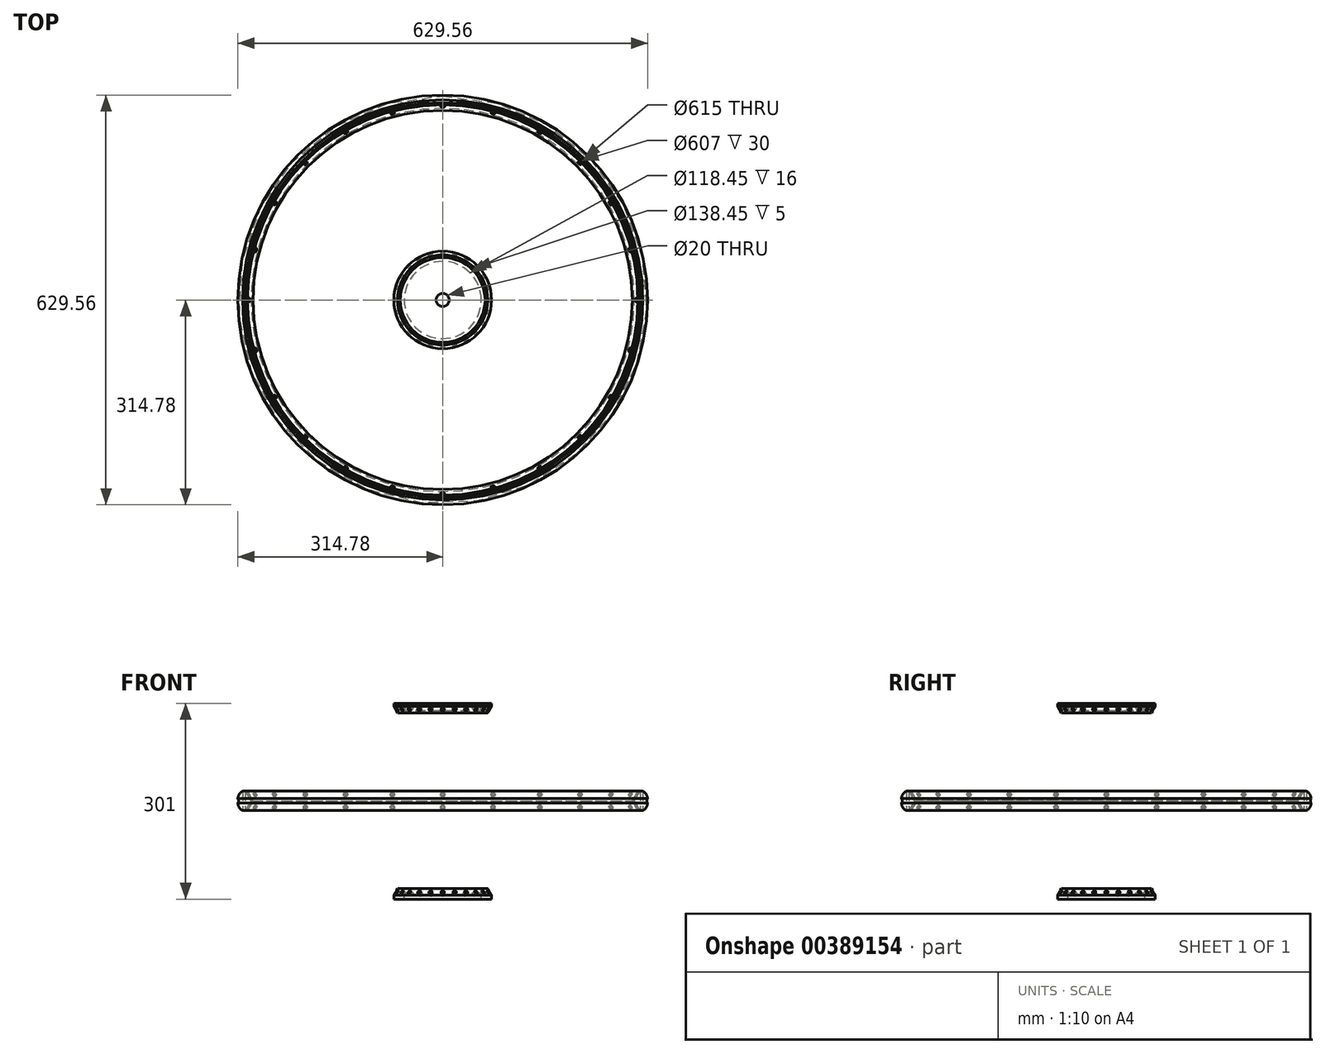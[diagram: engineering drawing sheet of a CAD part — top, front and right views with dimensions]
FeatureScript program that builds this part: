
annotation { "Feature Type Name" : "Feature", "Feature Type Description" : "" }
export const myFeature = defineFeature(function(context is Context, id is Id, definition is map)
    precondition{}
    {
        {
            var Q0;
            Q0=qCreatedBy(makeId("Front.planeOp"),FACE);
            var sketch = newSketch(context, id + "F0", { "sketchPlane" : qUnion([Q0])});
            skLineSegment(sketch, "E0.top", {"start": v(0, 135) * mm, "end": v(-69.23, 135) * mm});
            skLineSegment(sketch, "E0.left", {"start": v(0, 138) * mm, "end": v(0, 135) * mm});
            skLineSegment(sketch, "E1", {"start": v(-75, 145) * mm, "end": v(-69.23, 135) * mm});
            skLineSegment(sketch, "E2", {"start": v(-69.23, 145) * mm, "end": v(-65.19, 138) * mm});
            skLineSegment(sketch, "E3.top", {"start": v(-75, 150) * mm, "end": v(-69.23, 150) * mm});
            skLineSegment(sketch, "E3.left", {"start": v(-75, 145) * mm, "end": v(-75, 150) * mm});
            skLineSegment(sketch, "E3.right", {"start": v(-69.23, 145) * mm, "end": v(-69.23, 150) * mm});
            skLineSegment(sketch, "E4.top", {"start": v(0, 138) * mm, "end": v(-65.19, 138) * mm});
            skSolve(sketch);
        }
        {
            var Q0;
            Q0=makeQuery(id+"F0.imprint","IMPRINT",FACE,{"disambiguationData":[TD([[makeQuery(id+"F0.imprint","IMPRINT",EDGE,{"derivedFrom":sQuery(id+"F0.wireOp",EDGE,"E0.top")}),-1.0]])]});
            var Q1;
            Q1=sQuery(id+"F0.wireOp",EDGE,"E0.left");
            revolve(context, id + "F1", {"entities" : qUnion([Q0]), "axis" : qUnion([Q1]), "revolveType" : RevolveType.FULL});
        }
        {
            var Q0;
            Q0=qCreatedBy(makeId("Top.planeOp"),FACE);
            var sketch = newSketch(context, id + "F2", { "sketchPlane" : qUnion([Q0])});
            skCircle(sketch, "E5", {"center": v(0, 0) * mm, "radius": 10 * mm});
            skSolve(sketch);
        }
        {
            var Q0;
            Q0 = qSketchRegion(id + "F2", true);
            extrude(context, id + "F3", {"entities" : qUnion([Q0]), "operationType" : NewBodyOperationType.REMOVE, "oppositeDirection" : true, "depth" : 500 * mm, "symmetric" : true});
        }
        {
            var Q0;
            Q0=qCreatedBy(makeId("Front.planeOp"),FACE);
            var sketch = newSketch(context, id + "F4", { "sketchPlane" : qUnion([Q0])});
            skLineSegment(sketch, "E6.left", {"start": v(0, 0) * mm, "end": v(0, 10) * mm, "construction": true});
            skLineSegment(sketch, "E7", {"start": v(-300, 15) * mm, "end": v(-291.34, 0) * mm});
            skLineSegment(sketch, "E8", {"start": v(-291.34, 0) * mm, "end": v(-294.34, 0) * mm});
            skLineSegment(sketch, "E9", {"start": v(-294.34, 0) * mm, "end": v(-303, 15) * mm});
            skLineSegment(sketch, "E10", {"start": v(-303, 15) * mm, "end": v(-300, 15) * mm});
            skLineSegment(sketch, "E11.MirrorCS", {"start": v(-303, -15) * mm, "end": v(-300, -15) * mm});
            skLineSegment(sketch, "E12.MirrorCS", {"start": v(-294.34, 0) * mm, "end": v(-303, -15) * mm});
            skLineSegment(sketch, "E13.MirrorCS", {"start": v(-300, -15) * mm, "end": v(-291.34, 0) * mm});
            skSolve(sketch);
        }
        {
            var Q0;
            Q0=makeQuery(id+"F4.imprint","IMPRINT",FACE,{"disambiguationData":[TD([[makeQuery(id+"F4.imprint","IMPRINT",EDGE,{"derivedFrom":sQuery(id+"F4.wireOp",EDGE,"E7")}),-1.0]])]});
            var Q1;
            Q1=makeQuery(id+"F4.imprint","IMPRINT",FACE,{"disambiguationData":[TD([[makeQuery(id+"F4.imprint","IMPRINT",EDGE,{"derivedFrom":sQuery(id+"F4.wireOp",EDGE,"E8")}),1.0]])]});
            var Q2;
            Q2=sQuery(id+"F4.wireOp",EDGE,"E6.left");
            revolve(context, id + "F5", {"entities" : qUnion([Q0, Q1]), "axis" : qUnion([Q2]), "revolveType" : RevolveType.FULL});
        }
        {
            var Q0;
            Q0=qCreatedBy(makeId("Front.planeOp"),FACE);
            var sketch = newSketch(context, id + "F6", { "sketchPlane" : qUnion([Q0])});
            skLineSegment(sketch, "E14.top", {"start": v(-59.23, -145) * mm, "end": v(-75, -145) * mm});
            skLineSegment(sketch, "E14.left", {"start": v(0, -142) * mm, "end": v(0, -145) * mm});
            skLineSegment(sketch, "E15", {"start": v(-75, -145) * mm, "end": v(-69.23, -135) * mm});
            skLineSegment(sketch, "E16", {"start": v(-69.23, -135) * mm, "end": v(-59.23, -135) * mm});
            skLineSegment(sketch, "E17", {"start": v(-59.23, -135) * mm, "end": v(-59.23, -145) * mm});
            skLineSegment(sketch, "E18", {"start": v(-59.23, -145) * mm, "end": v(-59.23, -151) * mm});
            skLineSegment(sketch, "E19", {"start": v(-59.23, -151) * mm, "end": v(-75, -151) * mm});
            skLineSegment(sketch, "E20", {"start": v(-75, -151) * mm, "end": v(-75, -145) * mm});
            skSolve(sketch);
        }
        {
            var Q0;
            Q0=makeQuery(id+"F6.imprint","IMPRINT",FACE,{"disambiguationData":[TD([[makeQuery(id+"F6.imprint","IMPRINT",EDGE,{"derivedFrom":sQuery(id+"F6.wireOp",EDGE,"E14.top")}),-1.0]])]});
            var Q1;
            Q1=makeQuery(id+"F6.imprint","IMPRINT",FACE,{"disambiguationData":[TD([[makeQuery(id+"F6.imprint","IMPRINT",EDGE,{"derivedFrom":sQuery(id+"F6.wireOp",EDGE,"E14.top")}),1.0]])]});
            var Q2;
            Q2=sQuery(id+"F6.wireOp",EDGE,"E14.left");
            revolve(context, id + "F7", {"entities" : qUnion([Q0, Q1]), "axis" : qUnion([Q2]), "revolveType" : RevolveType.FULL});
        }
        {
            var Q0;
            Q0=qCreatedBy(makeId("Front.planeOp"),FACE);
            var sketch = newSketch(context, id + "F8", { "sketchPlane" : qUnion([Q0])});
            skLineSegment(sketch, "E21", {"start": v(24, 193.06) * mm, "end": v(22.75, 195.22) * mm});
            skLineSegment(sketch, "E22", {"start": v(22.75, 195.22) * mm, "end": v(-313.48, 1.1) * mm});
            skLineSegment(sketch, "E23", {"start": v(-313.48, 1.1) * mm, "end": v(-311.98, -1.5) * mm});
            skLineSegment(sketch, "E24", {"start": v(-311.98, -1.5) * mm, "end": v(24, 193.06) * mm});
            skLineSegment(sketch, "E25.MirrorCS", {"start": v(-313.48, -1.1) * mm, "end": v(-311.98, 1.5) * mm});
            skLineSegment(sketch, "E26.MirrorCS", {"start": v(-311.98, 1.5) * mm, "end": v(-65.2, -141.4) * mm});
            skLineSegment(sketch, "E27.MirrorCS", {"start": v(-66.51, -143.69) * mm, "end": v(-313.48, -1.1) * mm});
            skLineSegment(sketch, "E28", {"start": v(-66.51, -143.69) * mm, "end": v(-65.2, -141.4) * mm});
            skSolve(sketch);
        }
        {
            var Q0;
            {var subQ5=sQuery(id+"F8.wireOp",EDGE,"E21");Q0=makeQuery(id+"F8.imprint","IMPRINT",FACE,{"disambiguationData":[TD([[makeQuery(id+"F8.imprint","IMPRINT",EDGE,{"derivedFrom":subQ5}),1.0]])]});}
            var Q1;
            Q1=sQuery(id+"F8.wireOp",EDGE,"E22");
            revolve(context, id + "F9", {"entities" : qUnion([Q0]), "axis" : qUnion([Q1]), "revolveType" : RevolveType.FULL, "oppositeDirection" : true});
        }
        {
            var Q0;
            {var subQ0=sQuery(id+"F8.wireOp",EDGE,"E27.MirrorCS");Q0=makeQuery(id+"F8.imprint","IMPRINT",FACE,{"disambiguationData":[TD([[makeQuery(id+"F8.imprint","IMPRINT",EDGE,{"derivedFrom":subQ0}),-1.0]])]});}
            var Q1;
            Q1=sQuery(id+"F8.wireOp",EDGE,"E27.MirrorCS");
            revolve(context, id + "F10", {"entities" : qUnion([Q0]), "axis" : qUnion([Q1]), "revolveType" : RevolveType.FULL, "oppositeDirection" : true});
        }
        {
            var Q0;
            Q0=makeQuery(id+"F9.opRevolve","SWEPT_BODY",BODY,{"disambiguationData":[OSD([sQuery(id+"F8.wireOp",EDGE,"E21"),sQuery(id+"F8.wireOp",EDGE,"E22"),sQuery(id+"F8.wireOp",EDGE,"E23"),sQuery(id+"F8.wireOp",EDGE,"E24")])]});
            var Q1;
            Q1=makeQuery(id+"F10.opRevolve","SWEPT_BODY",BODY,{"disambiguationData":[OSD([sQuery(id+"F8.wireOp",EDGE,"E23"),sQuery(id+"F8.wireOp",EDGE,"E24"),sQuery(id+"F8.wireOp",EDGE,"4d24cdd7-ac5e-4949-9ab6-03e74b238c1a0.MirrorCS"),sQuery(id+"F8.wireOp",EDGE,"E25.MirrorCS"),sQuery(id+"F8.wireOp",EDGE,"E26.MirrorCS"),sQuery(id+"F8.wireOp",EDGE,"E27.MirrorCS")])]});
            var Q2;
            Q2=makeQuery(id+"F3.boolean.opBoolean","INTERSECT",EDGE,{"derivedFrom":[makeQuery(id+"F1.opRevolve","SWEPT_FACE",FACE,{"disambiguationData":[OSD([sQuery(id+"F0.wireOp",EDGE,"E0.top")])]}),makeQuery(id+"F3.opExtrude","SWEPT_FACE",FACE,{"disambiguationData":[OSD([sQuery(id+"F2.wireOp",EDGE,"E5")])]})]});
            circularPattern(context, id + "F11", {"operationType" : NewBodyOperationType.REMOVE, "entities" : qUnion([Q0, Q1]), "axis" : qUnion([Q2]), "angle" : 360 * degree, "instanceCount" : 24, "equalSpace" : true, "computeTransformsWithoutBuiltin" : true});
        }
        {
            var Q0;
            Q0=makeQuery(id+"F5.opRevolve","SWEPT_FACE",FACE,{"disambiguationData":[OSD([sQuery(id+"F4.wireOp",EDGE,"E11.MirrorCS")])]});
            var sketch = newSketch(context, id + "F12", { "sketchPlane" : qUnion([Q0])});
            skCircle(sketch, "E29", {"center": v(0, 0) * mm, "radius": 303.5 * mm});
            skCircle(sketch, "E30", {"center": v(0, 0) * mm, "radius": 307.5 * mm});
            skSolve(sketch);
        }
        {
            var Q0;
            Q0 = qSketchRegion(id + "F12", true);
            extrude(context, id + "F13", {"entities" : qUnion([Q0]), "oppositeDirection" : true, "depth" : 30 * mm});
        }
        {
            var Q0;
            Q0=qCreatedBy(makeId("Right.planeOp"),FACE);
            var sketch = newSketch(context, id + "F14", { "sketchPlane" : qUnion([Q0])});
            skPoint(sketch, "E31", {"position": v(307, 0) * mm});
            skLineSegment(sketch, "E32", {"start": v(307.5, 15) * mm, "end": v(307.5, 10.68) * mm});
            skLineSegment(sketch, "E33.MirrorCS", {"start": v(307.5, -15) * mm, "end": v(307.5, -10.68) * mm});
            skLineSegment(sketch, "E34", {"start": v(307.5, 10.68) * mm, "end": v(307.5, -10.68) * mm});
            skArc(sketch, "E35", {"start": v(314.78, 3.48) * mm, "mid": v(312.64, 10.2) * mm, "end": v(307.5, 15) * mm});
            skArc(sketch, "E36.MirrorCS", {"start": v(314.78, -3.48) * mm, "mid": v(312.64, -10.2) * mm, "end": v(307.5, -15) * mm});
            skArc(sketch, "E37", {"start": v(314.78, 3.48) * mm, "mid": v(313.6, 0) * mm, "end": v(314.78, -3.48) * mm});
            skSolve(sketch);
        }
        {
            var Q0;
            Q0=makeQuery(id+"F14.imprint","IMPRINT",FACE,{"disambiguationData":[TD([[makeQuery(id+"F14.imprint","IMPRINT",EDGE,{"derivedFrom":sQuery(id+"F14.wireOp",EDGE,"E32")}),1.0]])]});
            var Q1;
            Q1=makeQuery(id+"F13.opExtrude","CAP_EDGE",EDGE,{"disambiguationData":[OSD([sQuery(id+"F12.wireOp",EDGE,"E30")])],"isStart":false});
            sweep(context, id + "F15", {"operationType" : NewBodyOperationType.ADD, "profiles" : qUnion([Q0]), "path" : qUnion([Q1])});
        }
    });
